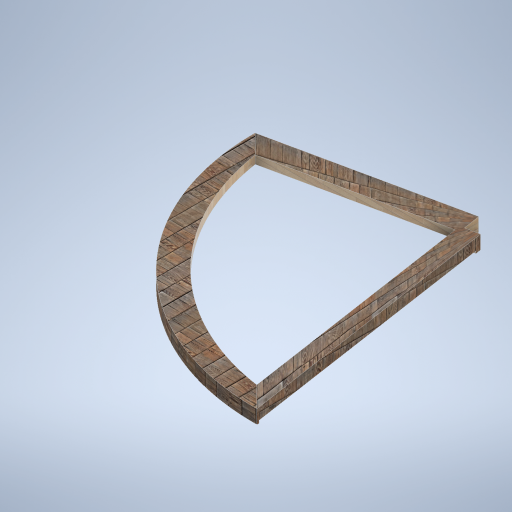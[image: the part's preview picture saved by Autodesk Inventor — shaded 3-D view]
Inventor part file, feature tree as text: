
AUTODESK INVENTOR PART (.ipt)
format: ipt  version: 2024.2 (Build 282272000, 272)  size: 643,584 bytes
history: native  units: in
note: dims shown in document units (in); Inventor stores cm internally (conversion verified against a paired STEP export)
features: sketch x32, extrude x15, projected_geometry x10, plane x7, other x5, loft x1
ambient origin geometry x8: Origin, YZ Plane, XZ Plane, XY Plane, X Axis, Y Axis, Z Axis, Center Point
bodies: Solid1 (feature_tree)
feature tree (70):
  other  "eave_frame_03.ipt"
  extrude  "Extrusion1"  Depth=102.3622in
  sketch  "Sketch16"  dims[d39=102.3622in d40=1.9685in d41=0.0in]
  extrude  "Extrusion2"  TaperAngle=0.0deg  [1 undecoded]
  extrude  "Extrusion3"  Depth=7.0866in TaperAngle=0.0deg
  extrude  "Extrusion4"  Depth=1.9685in TaperAngle=0.0deg
  extrude  "Extrusion5"  TaperAngle=90.0deg  [1 undecoded]
  sketch  "Sketch23"
  extrude  "Extrusion6"  Depth=0.0687in
  extrude  "Extrusion7"  Depth=1.1681in
  extrude  "Extrusion8"  Depth=1.9685in TaperAngle=0.0deg
  sketch  "Sketch26"
  extrude  "Extrusion9"  Depth=102.3622in
  sketch  "Sketch28"
  extrude  "Extrusion10"  Depth=1.9685in TaperAngle=0.0deg
  extrude  "Extrusion11"  Depth=102.3622in
  extrude  "Extrusion12"  Depth=1.9685in TaperAngle=0.0deg
  extrude  "Extrusion13"  TaperAngle=135.0deg  [1 undecoded]
  extrude  "Extrusion14"  TaperAngle=0.0deg  [1 undecoded]
  sketch  "Sketch34"
  sketch  "Sketch36"
  sketch  "Sketch37"
  plane  "Work Plane7"
  loft  "Loft1"
  extrude  "Extrusion15"  Depth=0.0344in
  other  "Solid1::eave_frame_03.ipt"
  other  "TaggingFeature1"
  sketch  "Sketch1"  dims[d0=0.3937in d4=102.3622in]
  sketch  "Sketch2"  dims[d5=1.1811in d6=0.0in d7=0.0in]
  sketch  "Sketch5"  dims[d8=0.0687in d9=7.0866in d10=0.0in]
  sketch  "Sketch6"  dims[d11=7.0866in d12=0.0in d13=1.9685in d14=0.0in]
  sketch  "Sketch7"  dims[d15=1.9685in d16=0.0in d17=90.0deg]
  sketch  "Sketch8"  dims[d18=0.3937in d19=0.0in d20=0.0687in]
  sketch  "Sketch9"  dims[d21=0.0in d22=0.0in d24=1.1681in]
  sketch  "Sketch10"  dims[d25=0.0in d26=0.0in d27=1.9685in d28=0.0in]
  sketch  "Sketch11"  dims[d30=1.9685in d31=0.0in d32=102.3622in]
  sketch  "Sketch12"  dims[d33=102.3622in d34=1.9685in d35=0.0in]
  plane  "Work Plane1"
  plane  "Work Plane2"
  plane  "Work Plane3"
  plane  "Work Plane4"
  plane  "Work Plane5"
  plane  "Work Plane6"
  sketch  "Sketch15"  dims[d36=1.9685in d37=0.0in d38=102.3622in]
  sketch  "Sketch19"  dims[d42=1.9685in d43=0.0in d44=135.0deg]
  projected_geometry  "Projected Loop1"
  sketch  "Sketch20"  dims[d46=0.0in d47=90.0deg d48=0.0in d49=90.0deg]
  sketch  "Sketch21"  dims[d50=0.0in d51=90.0deg d52=1.378in d53=0.0in]
  sketch  "Sketch22"  dims[d29=19.685in d45=0.0344in]
  projected_geometry  "Projected Loop2"
  sketch  "Sketch24"
  sketch  "Sketch25"
  projected_geometry  "Projected Loop3"
  sketch  "Sketch27"
  sketch  "Sketch29"
  sketch  "Sketch30"
  projected_geometry  "Projected Loop4"
  sketch  "Sketch31"
  projected_geometry  "Projected Loop5"
  sketch  "Sketch32"
  sketch  "Sketch33"
  projected_geometry  "Projected Loop6"
  projected_geometry  "Projected Loop7"
  projected_geometry  "Projected Loop8"
  projected_geometry  "Projected Loop9"
  sketch  "Sketch38"
  other  "Edges1"
  other  "Edges2"
  sketch  "Sketch40"
  projected_geometry  "Projected Loop10"
note: 4 required parameter values undecoded (feature->parameter linkage not recoverable at this tier; creation-order binding heuristic only, values carry confidence <= 0.55)
